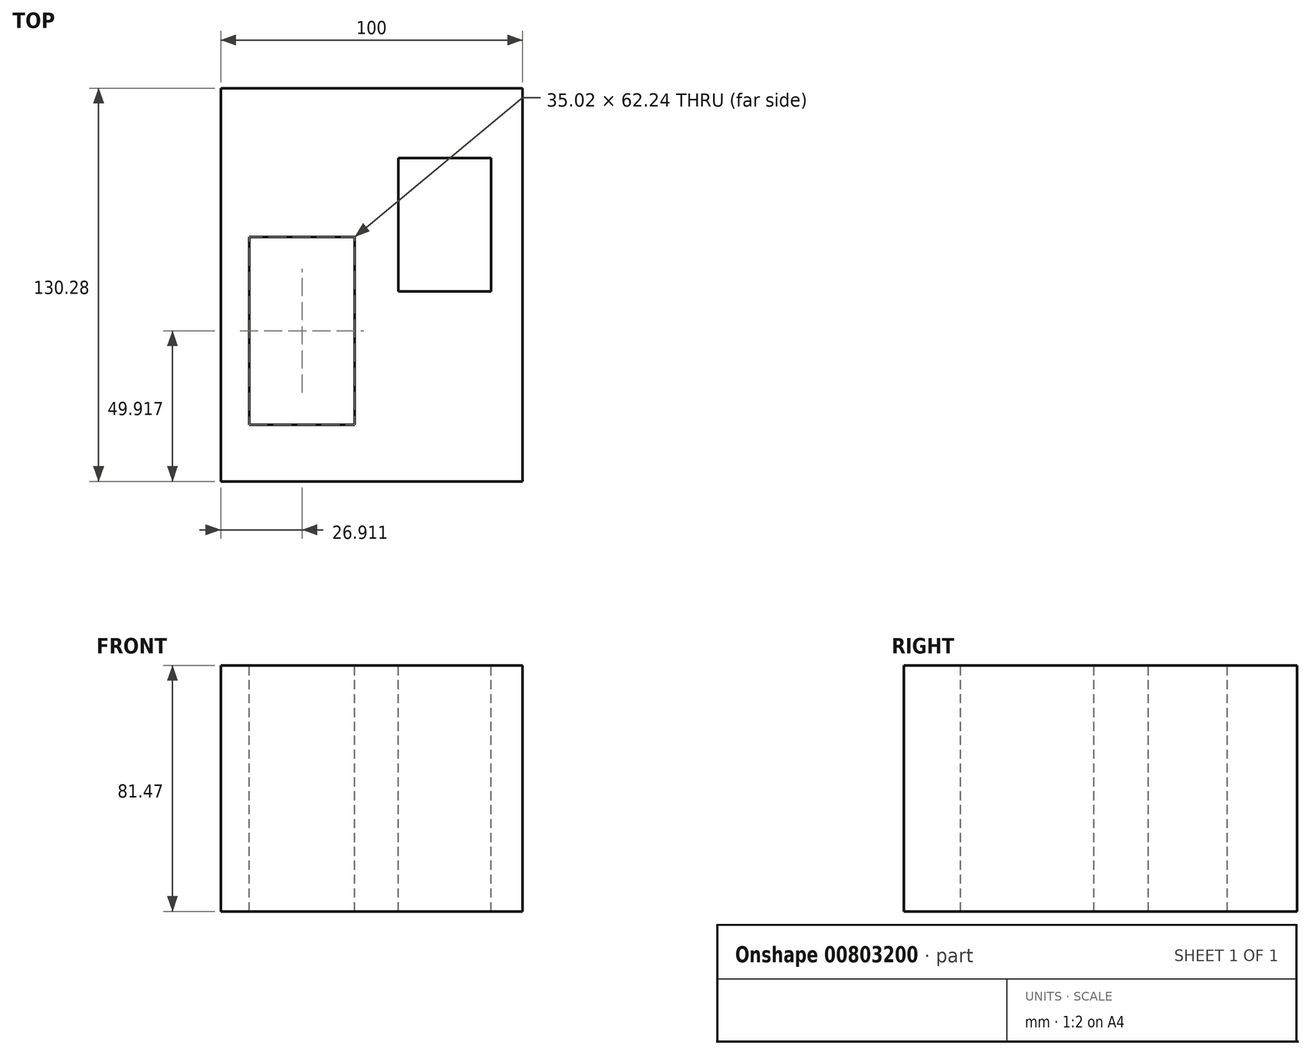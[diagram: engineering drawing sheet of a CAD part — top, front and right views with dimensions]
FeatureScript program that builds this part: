
annotation { "Feature Type Name" : "Feature", "Feature Type Description" : "" }
export const myFeature = defineFeature(function(context is Context, id is Id, definition is map)
    precondition{}
    {
        {
            var Q0;
            Q0=qCreatedBy(makeId("Right.planeOp"),FACE);
            var sketch = newSketch(context, id + "F0", { "sketchPlane" : qUnion([Q0])});
            skLineSegment(sketch, "E0.bottom", {"start": v(-66.32, 38.38) * mm, "end": v(63.96, 38.38) * mm});
            skLineSegment(sketch, "E0.top", {"start": v(-66.32, -43.1) * mm, "end": v(63.96, -43.1) * mm});
            skLineSegment(sketch, "E0.left", {"start": v(-66.32, 38.38) * mm, "end": v(-66.32, -43.1) * mm});
            skLineSegment(sketch, "E0.right", {"start": v(63.96, 38.38) * mm, "end": v(63.96, -43.1) * mm});
            skSolve(sketch);
        }
        {
            var Q0;
            Q0=makeQuery(id+"F0.imprint","IMPRINT",FACE,{"disambiguationData":[TD([[makeQuery(id+"F0.imprint","IMPRINT",EDGE,{"derivedFrom":sQuery(id+"F0.wireOp",EDGE,"E0.bottom")}),-1.0]])]});
            extrude(context, id + "F1", {"entities" : qUnion([Q0]), "depth" : 100 * mm, "offsetDistance" : 25 * mm});
        }
        {
            var Q0;
            Q0=makeQuery(id+"F1.opExtrude","SWEPT_FACE",FACE,{"disambiguationData":[OSD([sQuery(id+"F0.wireOp",EDGE,"E0.bottom")])]});
            var sketch = newSketch(context, id + "F2", { "sketchPlane" : qUnion([Q0])});
            skLineSegment(sketch, "E1.bottom", {"start": v(9.4, -47.52) * mm, "end": v(44.42, -47.52) * mm});
            skLineSegment(sketch, "E1.top", {"start": v(9.4, 14.72) * mm, "end": v(44.42, 14.72) * mm});
            skLineSegment(sketch, "E1.left", {"start": v(9.4, -47.52) * mm, "end": v(9.4, 14.72) * mm});
            skLineSegment(sketch, "E1.right", {"start": v(44.42, -47.52) * mm, "end": v(44.42, 14.72) * mm});
            skLineSegment(sketch, "E2.bottom", {"start": v(58.8, -3.32) * mm, "end": v(89.54, -3.32) * mm});
            skLineSegment(sketch, "E2.top", {"start": v(58.8, 40.8) * mm, "end": v(89.54, 40.8) * mm});
            skLineSegment(sketch, "E2.left", {"start": v(58.8, -3.32) * mm, "end": v(58.8, 40.8) * mm});
            skLineSegment(sketch, "E2.right", {"start": v(89.54, -3.32) * mm, "end": v(89.54, 40.8) * mm});
            skSolve(sketch);
        }
        {
            var Q0;
            Q0=makeQuery(id+"F2.imprint","IMPRINT",FACE,{"disambiguationData":[TD([[makeQuery(id+"F2.imprint","IMPRINT",EDGE,{"derivedFrom":sQuery(id+"F2.wireOp",EDGE,"E1.bottom")}),1.0]])]});
            extrude(context, id + "F3", {"entities" : qUnion([Q0]), "operationType" : NewBodyOperationType.REMOVE, "oppositeDirection" : true, "depth" : 100 * mm, "offsetDistance" : 25 * mm});
        }
        {
            var Q0;
            Q0=makeQuery(id+"F2.imprint","IMPRINT",FACE,{"disambiguationData":[TD([[makeQuery(id+"F2.imprint","IMPRINT",EDGE,{"derivedFrom":sQuery(id+"F2.wireOp",EDGE,"E2.bottom")}),1.0]])]});
            extrude(context, id + "F4", {"entities" : qUnion([Q0]), "operationType" : NewBodyOperationType.REMOVE, "oppositeDirection" : true, "depth" : 100 * mm, "offsetDistance" : 25 * mm});
        }
    });
